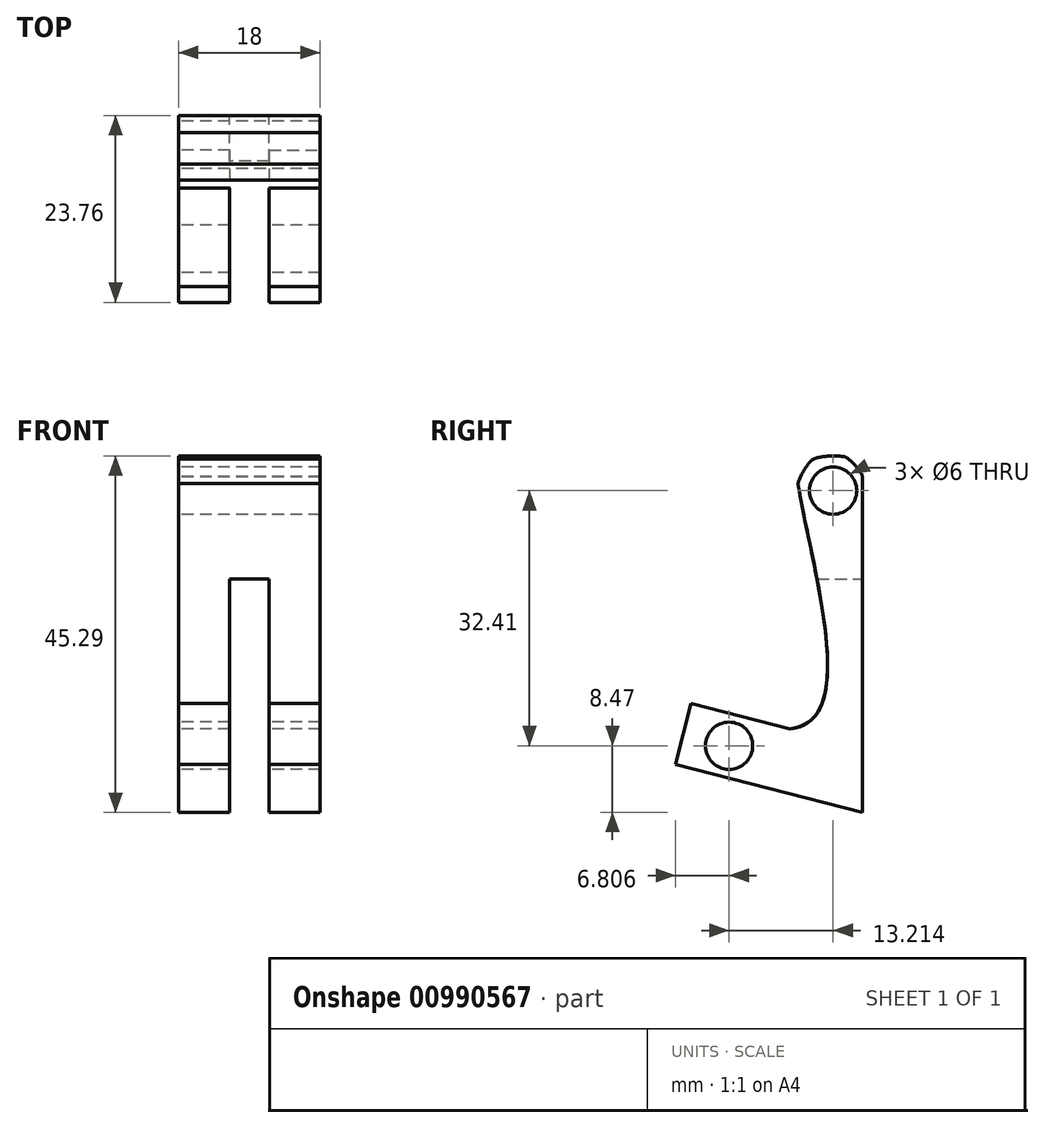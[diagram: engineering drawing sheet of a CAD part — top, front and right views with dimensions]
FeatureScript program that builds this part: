
annotation { "Feature Type Name" : "Feature", "Feature Type Description" : "" }
export const myFeature = defineFeature(function(context is Context, id is Id, definition is map)
    precondition{}
    {
        {
            var Q0;
            Q0=qCreatedBy(makeId("Right.planeOp"),FACE);
            var sketch = newSketch(context, id + "F0", { "sketchPlane" : qUnion([Q0])});
            skLineSegment(sketch, "E0", {"start": v(-0.5, -36.26) * mm, "end": v(-13.03, -33.05) * mm});
            skLineSegment(sketch, "E1", {"start": v(-13.03, -33.05) * mm, "end": v(-15.02, -40.8) * mm});
            skLineSegment(sketch, "E2", {"start": v(-15.02, -40.8) * mm, "end": v(10, -47.2) * mm});
            skLineSegment(sketch, "E3", {"start": v(10, -47.2) * mm, "end": v(10, 0) * mm});
            skLineSegment(sketch, "E4", {"start": v(10, 0) * mm, "end": v(0, 0) * mm});
            skCircle(sketch, "E5", {"center": v(5, -6) * mm, "radius": 3 * mm});
            skPoint(sketch, "E5.centerSnap0", {"position": v(5, 0) * mm});
            skLineSegment(sketch, "E6", {"start": v(-14.03, -36.92) * mm, "end": v(10, -43.08) * mm, "construction": true});
            skCircle(sketch, "E7", {"center": v(-8.21, -38.4) * mm, "radius": 3 * mm});
            skFitSpline(sketch, "E8", {"points": [v(0, 0) * mm, v(-0.5, -36.26) * mm], "startDerivative": vector(0, -29.4) * mm, "endDerivative": vector(-31.5, -2.9) * mm});
            skSolve(sketch);
        }
        {
            var Q0;
            Q0=makeQuery(id+"F0.imprint","IMPRINT",FACE,{"disambiguationData":[TD([[makeQuery(id+"F0.imprint","IMPRINT",EDGE,{"derivedFrom":sQuery(id+"F0.wireOp",EDGE,"E0")}),1.0]])]});
            extrude(context, id + "F1", {"entities" : qUnion([Q0]), "depth" : 18 * mm, "offsetDistance" : 25.4 * mm});
        }
        {
            var Q0;
            Q0=makeQuery(id+"F1.opExtrude","SWEPT_FACE",FACE,{"disambiguationData":[OSD([sQuery(id+"F0.wireOp",EDGE,"E3")])]});
            var sketch = newSketch(context, id + "F2", { "sketchPlane" : qUnion([Q0])});
            skLineSegment(sketch, "E9", {"start": v(-11.5, -47.2) * mm, "end": v(-11.5, -17.2) * mm});
            skLineSegment(sketch, "E10", {"start": v(-11.5, -17.2) * mm, "end": v(-6.5, -17.2) * mm});
            skLineSegment(sketch, "E11", {"start": v(-6.5, -17.2) * mm, "end": v(-6.5, -47.2) * mm});
            skLineSegment(sketch, "E12", {"start": v(-18, -47.2) * mm, "end": v(-11.5, -47.2) * mm});
            skLineSegment(sketch, "E13", {"start": v(-6.5, -47.2) * mm, "end": v(0, -47.2) * mm});
            skSolve(sketch);
        }
        {
            var Q0;
            {var subQ0=sQuery(id+"F2.wireOp",EDGE,"E9");Q0=makeQuery(id+"F2.imprint","IMPRINT",FACE,{"disambiguationData":[TD([[makeQuery(id+"F2.imprint","IMPRINT",EDGE,{"derivedFrom":subQ0}),-1.0]])]});}
            extrude(context, id + "F3", {"entities" : qUnion([Q0]), "operationType" : NewBodyOperationType.REMOVE, "oppositeDirection" : true, "depth" : 25.4 * mm, "offsetDistance" : 25.4 * mm});
        }
        {
            var Q0;
            Q0=qCreatedBy(makeId("Right.planeOp"),FACE);
            var sketch = newSketch(context, id + "F4", { "sketchPlane" : qUnion([Q0])});
            skFitSpline(sketch, "E14", {"points": [v(0, -3.46) * mm, v(10, -3.38) * mm], "startDerivative": vector(6.05, 7) * mm, "endDerivative": vector(7, -7.65) * mm});
            skLineSegment(sketch, "E15", {"start": v(10, -3.38) * mm, "end": v(10, 0) * mm});
            skLineSegment(sketch, "E16", {"start": v(10, 0) * mm, "end": v(0, 0) * mm});
            skLineSegment(sketch, "E17", {"start": v(0, 0) * mm, "end": v(10, 0) * mm});
            skLineSegment(sketch, "E18", {"start": v(0, 0) * mm, "end": v(0, -3.46) * mm});
            skSolve(sketch);
        }
        {
            var Q0;
            Q0=makeQuery(id+"F4.imprint","IMPRINT",FACE,{"disambiguationData":[TD([[makeQuery(id+"F4.imprint","IMPRINT",EDGE,{"derivedFrom":sQuery(id+"F4.wireOp",EDGE,"E14")}),1.0]])]});
            var Q1;
            Q1=makeQuery(id+"F1.opExtrude","CAP_FACE",FACE,{"disambiguationData":[OSD([sQuery(id+"F0.wireOp",EDGE,"E0"),sQuery(id+"F0.wireOp",EDGE,"E1"),sQuery(id+"F0.wireOp",EDGE,"E2"),sQuery(id+"F0.wireOp",EDGE,"E3"),sQuery(id+"F0.wireOp",EDGE,"E4"),sQuery(id+"F0.wireOp",EDGE,"E5"),sQuery(id+"F0.wireOp",EDGE,"E7"),sQuery(id+"F0.wireOp",EDGE,"E8")])],"isStart":false});
            extrude(context, id + "F5", {"entities" : qUnion([Q0, Q1]), "operationType" : NewBodyOperationType.REMOVE, "depth" : 50.8 * mm, "offsetDistance" : 25.4 * mm});
        }
        {
            var Q0;
            Q0=qCreatedBy(makeId("Right.planeOp"),FACE);
            var sketch = newSketch(context, id + "F6", { "sketchPlane" : qUnion([Q0])});
            skLineSegment(sketch, "E19.bottom", {"start": v(8.74, -2.18) * mm, "end": v(10.5, -2.18) * mm});
            skLineSegment(sketch, "E19.top", {"start": v(8.74, -47.83) * mm, "end": v(10.5, -47.83) * mm});
            skLineSegment(sketch, "E19.left", {"start": v(8.74, -2.18) * mm, "end": v(8.74, -47.83) * mm});
            skLineSegment(sketch, "E19.right", {"start": v(10.5, -2.18) * mm, "end": v(10.5, -47.83) * mm});
            skSolve(sketch);
        }
        {
            var Q0;
            Q0 = qSketchRegion(id + "F6", true);
            extrude(context, id + "F7", {"entities" : qUnion([Q0]), "operationType" : NewBodyOperationType.REMOVE, "depth" : 50.8 * mm, "offsetDistance" : 25.4 * mm});
        }
        {
            var Q0;
            Q0=qCreatedBy(makeId("Right.planeOp"),FACE);
            var sketch = newSketch(context, id + "F8", { "sketchPlane" : qUnion([Q0])});
            skFitSpline(sketch, "E20", {"points": [v(2.7, -1.88) * mm, v(0.48, -5.26) * mm], "startDerivative": vector(-2.72, -1.03) * mm, "endDerivative": vector(-0.44, -2.28) * mm});
            skLineSegment(sketch, "E21", {"start": v(2.7, -1.88) * mm, "end": v(-0.07, -2.75) * mm});
            skLineSegment(sketch, "E22", {"start": v(-0.07, -2.75) * mm, "end": v(0.48, -5.26) * mm});
            skFitSpline(sketch, "E23", {"points": [v(6.5, -1.68) * mm, v(8.73, -4.25) * mm], "startDerivative": vector(2, -0.83) * mm, "endDerivative": vector(0.3, -1.95) * mm});
            skLineSegment(sketch, "E24", {"start": v(6.5, -1.68) * mm, "end": v(8.9, -2.13) * mm});
            skLineSegment(sketch, "E25", {"start": v(8.9, -2.13) * mm, "end": v(8.73, -4.25) * mm});
            skSolve(sketch);
        }
        {
            var Q0;
            Q0=makeQuery(id+"F8.imprint","IMPRINT",FACE,{"disambiguationData":[TD([[makeQuery(id+"F8.imprint","IMPRINT",EDGE,{"derivedFrom":sQuery(id+"F8.wireOp",EDGE,"E23")}),1.0]])]});
            var Q1;
            Q1=makeQuery(id+"F8.imprint","IMPRINT",FACE,{"disambiguationData":[TD([[makeQuery(id+"F8.imprint","IMPRINT",EDGE,{"derivedFrom":sQuery(id+"F8.wireOp",EDGE,"E20")}),-1.0]])]});
            extrude(context, id + "F9", {"entities" : qUnion([Q0, Q1]), "operationType" : NewBodyOperationType.REMOVE, "depth" : 50.8 * mm, "offsetDistance" : 25.4 * mm});
        }
    });
